# Revit family: ШУВ-М_С300_РЖ_ЮТ_18.03.25
name_source: partatom
category: Оборудование
units: mm (PartAtom-declared; Revit-internal decimal feet)

## family parameters
Всегда вертикально = Да
Классификация = Нет
На основе рабочей плоскости = Нет
Общий = Нет
При загрузке вырезать с полостями = Нет
Размер круглого соединителя = Использовать диаметр
Тип детали = Нормальный
Точка расчета площади = Нет

## types (5) — shared parameters
URL = https://plazma-t.ru
Группа модели = ШУВ-М
Изготовитель = ООО "Плазма-Т"
Назв гориз ПУШ = 210 мм
Расст ввод от задней стенки = 60 мм
zero-valued in all types: Отметка по умолчанию

## per-type parameters (varying)
| type | A | B | Комментарии к типоразмеру | Расст ПУШ от верхней стенки | Расст ПУШ от левой стенки | Расст ввод от левой стенки | Расст замок | Типоразмер шкафа | расст замок верт |
| ШУВ-М_С300_РЖ_ЮТ_37-45кВт | 225 мм | 250 мм | Ш4/DEK | 110 мм | 335 мм | 355 мм | 55 мм | Ш4 | 400 мм |
| ШУВ-М_С300_РЖ_ЮТ_90кВт | 275 мм | 300 мм | Ш6/DEK | 190 мм | 355 мм | 400 мм | 55 мм | Ш6 | 480 мм |
| ШУВ-М_С300_РЖ_ЮТ_18,5-30кВт | 150 мм | 175 мм | Ш3/DEK | 110 мм | 220 мм | 360 мм | 55 мм | Ш3 | 300 мм |
| ШУВ-М_С300_РЖ_ЮТ_55-75кВт | 225 мм | 250 мм | Ш5/DEK | 190 мм | 355 мм | 440 мм | 70 мм | Ш5 | 480 мм |
| ШУВ-М_С300_РЖ_ЮТ_1,5-15кВт | 100 мм | 125 мм | Ш2/DEK | 80 мм | 160 мм | 320 мм | 55 мм | Ш2 | 250 мм |
